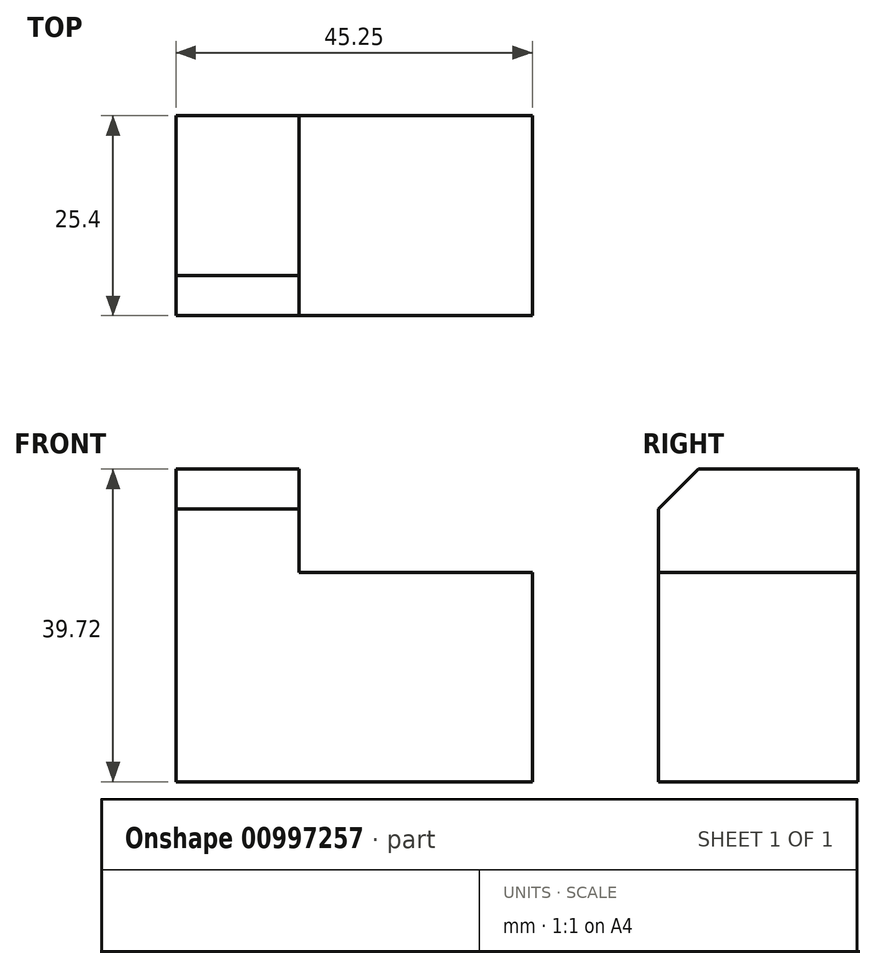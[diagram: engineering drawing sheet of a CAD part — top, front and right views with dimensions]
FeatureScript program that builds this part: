
annotation { "Feature Type Name" : "Feature", "Feature Type Description" : "" }
export const myFeature = defineFeature(function(context is Context, id is Id, definition is map)
    precondition{}
    {
        {
            var Q0;
            Q0=qCreatedBy(makeId("Front.planeOp"),FACE);
            var sketch = newSketch(context, id + "F0", { "sketchPlane" : qUnion([Q0])});
            skLineSegment(sketch, "E0", {"start": v(0, 0) * mm, "end": v(45.25, 0) * mm});
            skLineSegment(sketch, "E1", {"start": v(45.25, 0) * mm, "end": v(45.25, 26.57) * mm});
            skLineSegment(sketch, "E2", {"start": v(45.25, 26.57) * mm, "end": v(15.62, 26.57) * mm});
            skLineSegment(sketch, "E3", {"start": v(15.62, 26.57) * mm, "end": v(15.62, 39.72) * mm});
            skLineSegment(sketch, "E4", {"start": v(15.62, 39.72) * mm, "end": v(0, 39.72) * mm});
            skLineSegment(sketch, "E5", {"start": v(0, 39.72) * mm, "end": v(0, 0) * mm});
            skSolve(sketch);
        }
        {
            var Q0;
            Q0=makeQuery(id+"F0.imprint","IMPRINT",FACE,{"disambiguationData":[TD([[makeQuery(id+"F0.imprint","IMPRINT",EDGE,{"derivedFrom":sQuery(id+"F0.wireOp",EDGE,"E0")}),1.0]])]});
            extrude(context, id + "F1", {"entities" : qUnion([Q0]), "depth" : 25.4 * mm, "offsetDistance" : 25.4 * mm});
        }
        {
            var Q0;
            Q0=makeQuery(id+"F1.opExtrude","CAP_EDGE",EDGE,{"disambiguationData":[OSD([sQuery(id+"F0.wireOp",EDGE,"E4")])],"isStart":false});
            chamfer(context, id + "F2", {"entities" : qUnion([Q0]), "width" : 5.08 * mm, "tangentPropagation" : true});
        }
    });
